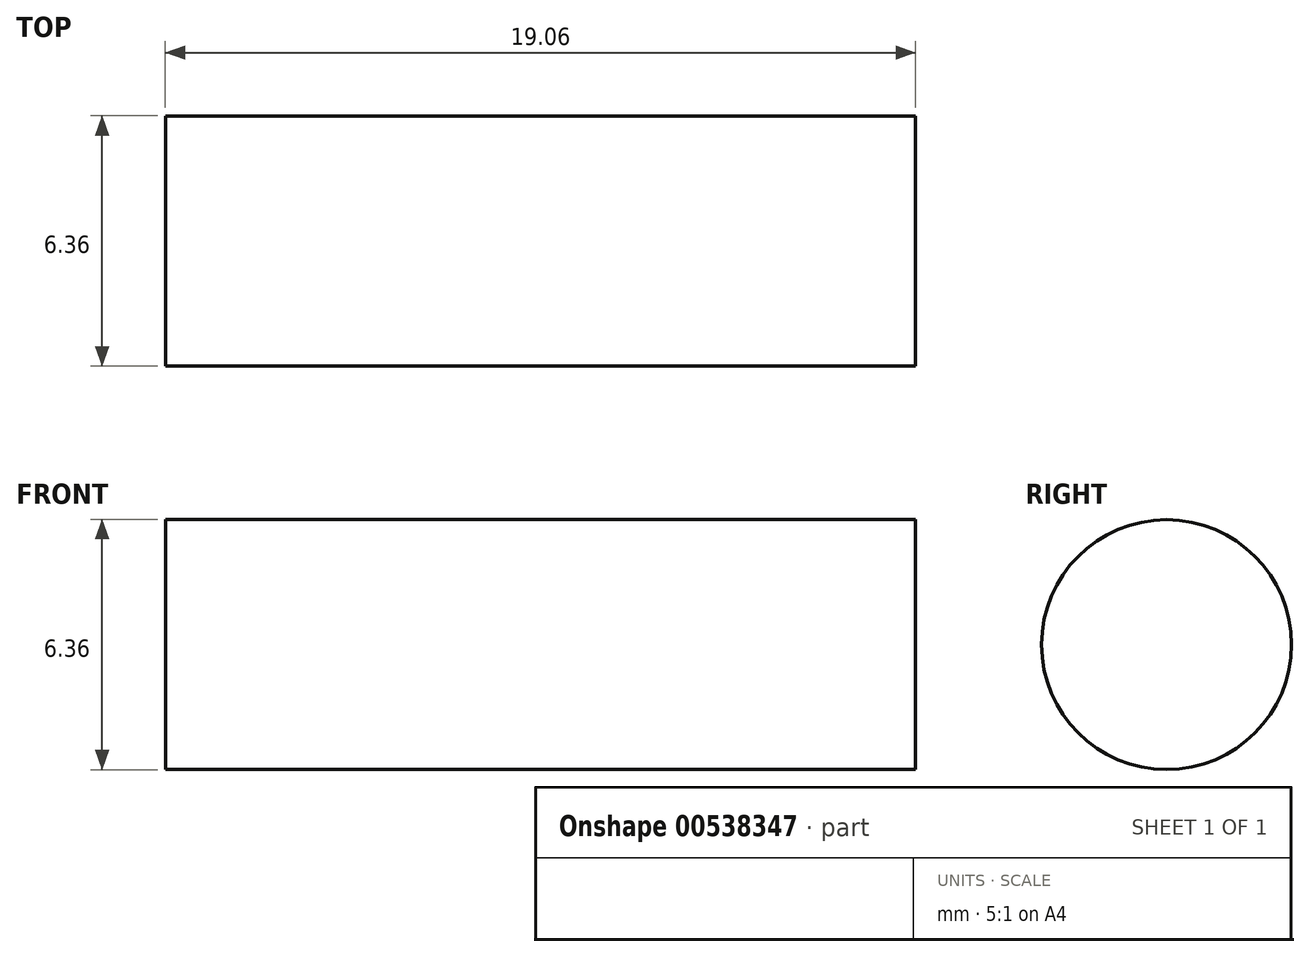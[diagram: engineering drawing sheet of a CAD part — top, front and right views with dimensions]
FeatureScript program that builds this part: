
annotation { "Feature Type Name" : "Feature", "Feature Type Description" : "" }
export const myFeature = defineFeature(function(context is Context, id is Id, definition is map)
    precondition{}
    {
        {
            var Q0;
            Q0=qCreatedBy(makeId("Right.planeOp"),FACE);
            var sketch = newSketch(context, id + "F0", { "sketchPlane" : qUnion([Q0])});
            skCircle(sketch, "E0", {"center": v(0, 0) * mm, "radius": 3.18 * mm});
            skSolve(sketch);
        }
        {
            var Q0;
            Q0 = qSketchRegion(id + "F0", true);
            extrude(context, id + "F1", {"entities" : qUnion([Q0]), "endBound" : BoundingType.SYMMETRIC, "depth" : 19.05 * mm, "offsetDistance" : 25.4 * mm});
        }
    });
